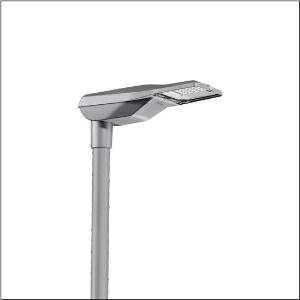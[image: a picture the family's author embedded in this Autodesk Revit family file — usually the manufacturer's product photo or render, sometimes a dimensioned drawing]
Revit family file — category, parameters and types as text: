
# Revit family: streetlight_sl_21_iq_micro___st1_5a_5xe1p31g08db_6e7e
name_source: partatom
category: Lighting Fixtures
units: mm (PartAtom-declared; Revit-internal decimal feet)

## family parameters
Cut with Voids When Loaded = No
Host = Face
Light Source = No
Part Type = Normal
Room Calculation Point = No
Round Connector Dimension = Use Diameter
Shared = No

## types (1)
- --- (1 x LED, 4730 lm, 36.4 W, 3000K)
    Apparent Load = 36 VA
    CIE Flux Codes = 22 53 95 100 100
    Color Rendering = 70
    Color Temperature = 3000K
    Default Elevation = 1800 mm
    Description = Streetlight SL 21 iQ micro, mast luminaire, primary light control with lens, of PMMA, primary optical cover: cover, of toughened safety glass, transparent, light distribution: ST1.5a, light emission: direct distribution, primary light characteristic: asymmetric, installation type: post-top, side-entry, LED, High Power LED, rated luminous flux: 4.730lm, luminous efficacy: 130lm/W, light colour: 730, colour temperature: 3000K, control: Street-Remote, Auto-Match, Temp-Guard, Lumen-Switch, Night-Set, Smart-Wire, Light-Fading, Desk-Remote (wireless, voltage-free reading and setting of iQ features in the workshop via application-optimized NFC function/RFID function), optimised constant luminous flux control (CLO 2.0), presetting dimming linear, mains connection: 220..240V, AC, 50/60Hz, start of lifetime: 36W, end of service life: 38W, reduction: 16W, luminaire housing, of diecast aluminium, powder-coated, Siteco® metallic grey (DB 702S), corrosivity category C5 mid according to DIN EN ISO 12944, please order mast flange separately, inclination adjustable: 0°, 5°, 10°, 15°, sealing non-destructively replaceable, multi-level sealing system, length: 528mm, width: 235mm, height: 110mm, mast flange for spigot size: 42mm (side-entry): 5XC10008XM4, 60/48mm (side-entry/post-top): 5XC10108XM2, 76/60mm (side-entry/post-top): 5XC10108XM1, protection rating (complete): IP66, insulation class (complete): insulation class II (safety insulation), certification: CE, ENEC, ENEC+, VDE, impact resistance: IK09, permissible operating ambient temperature for outdoor applications: -40..+50°C, standard-compliant lighting for roads and squares, packaging unit: 1 piece

Light Distribution: ST1.5a
    Height = 110 mm
    Lamp = 1 x LED
    Lamp Light Flux = 4730 lm
    Lamp Power = 36.4 W
    Lamp count = 1
    Length = 528 mm
    Luminous efficacy = 130 lm/W
    Manufacturer = Siteco
    ModVariant = No
    Model = 5XE1P31G08DB
    Number of Poles = 1
    OnlyDefault = Yes
    Power Factor = 1
    Product Name = Streetlight SL 21 iQ micro | ST1.5a
    Product group = mast luminaire | pylon top
    ProductGroupID = 6100
    Protection Class = Protection class II
    Protection Degree = IP 66
    RLX_Detail_Level = 1
    RLX_Emergency_Light_Flux = 0 lm
    RLX_Emergency_Type = 0
    RLX_Emergency_Type_DB = No
    RlxData = <blob elided: 103205 chars, md5=5e39fe7e>
    Socket = socket
    Standby Power = 0 W
    System Light Flux = 4730 lm
    System Power = 36 W
    Type Comments = factory setting: luminous flux: 100 % | dim-lin: 254 | 715 mA
    Type Image = l_1006881.jpg
    URL = http://relux.com
    VarID = @adj_086167
    Voltage = 0 V
    Weight = 0.00 kg
    Width = 235 mm

## geometry (parser evidence)
native form markers: Blend x4, Sweep x12
no freeform markers — native parametric forms only
